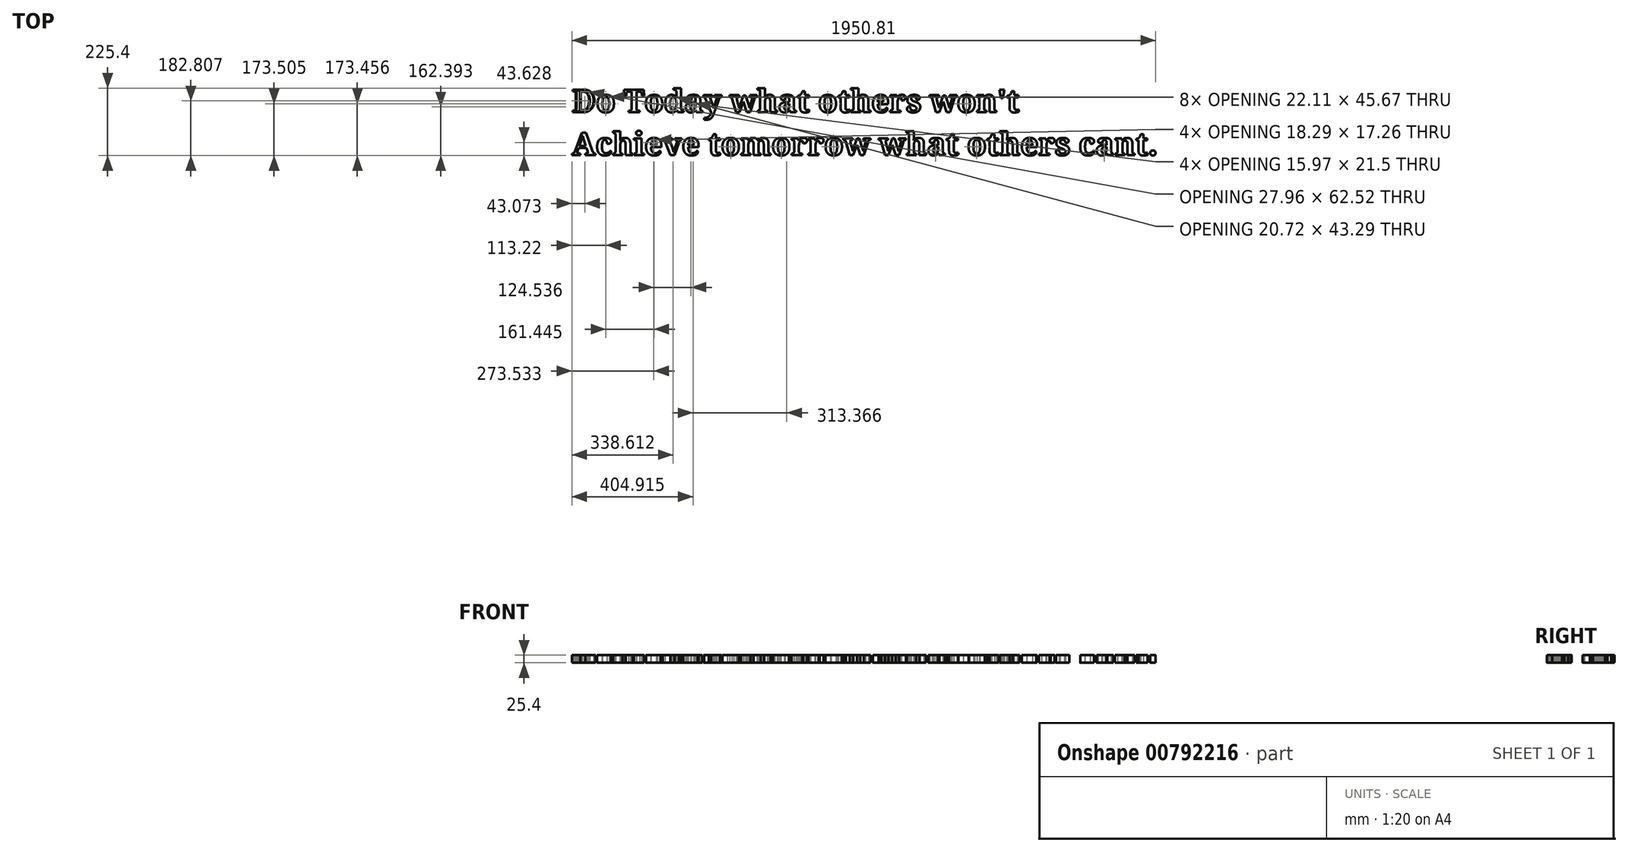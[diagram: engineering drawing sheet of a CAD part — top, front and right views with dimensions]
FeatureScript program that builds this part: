
annotation { "Feature Type Name" : "Feature", "Feature Type Description" : "" }
export const myFeature = defineFeature(function(context is Context, id is Id, definition is map)
    precondition{}
    {
        {
            var Q0;
            Q0=qCreatedBy(makeId("Top.planeOp"),FACE);
            var sketch = newSketch(context, id + "F0", { "sketchPlane" : qUnion([Q0])});
            skLineSegment(sketch, "E0.bottom", {"start": v(979.04, 38.1) * mm, "end": v(-979.04, 38.1) * mm, "construction": true});
            skLineSegment(sketch, "E0.top", {"start": v(979.04, -38.1) * mm, "end": v(-979.04, -38.1) * mm, "construction": true});
            skLineSegment(sketch, "E0.left", {"start": v(979.04, 38.1) * mm, "end": v(979.04, -38.1) * mm, "construction": true});
            skLineSegment(sketch, "E0.right", {"start": v(-979.04, 38.1) * mm, "end": v(-979.04, -38.1) * mm, "construction": true});
            skPoint(sketch, "E0.middle", {"position": v(0, 0) * mm});
            skText(sketch, "E1", { "text": "Do Today what others won\'t\nAchieve tomorrow what others cant.", "fontName": "NotoSerif-Bold.ttf"});
            const initialGuessF0  = {"E1": [-0.97904, -0.0381, 1, 0, 0.0762]};
            skSetInitialGuess(sketch, initialGuessF0);
            skSolve(sketch);
        }
        {
            var Q0;
            Q0 = qSketchRegion(id + "F0", true);
            extrude(context, id + "F1", {"entities" : qUnion([Q0]), "depth" : 25.4 * mm, "offsetDistance" : 25.4 * mm});
        }
        {
            var Q0;
            Q0=makeQuery(id+"F1.opExtrude","CAP_FACE",FACE,{"disambiguationData":[OSD([sQuery(id+"F0.wireOp",EDGE,"E1.sketch_text.stroke-0"),sQuery(id+"F0.wireOp",EDGE,"E1.sketch_text.stroke-1"),sQuery(id+"F0.wireOp",EDGE,"E1.sketch_text.stroke-2"),sQuery(id+"F0.wireOp",EDGE,"E1.sketch_text.stroke-3"),sQuery(id+"F0.wireOp",EDGE,"E1.sketch_text.stroke-4"),sQuery(id+"F0.wireOp",EDGE,"E1.sketch_text.stroke-5"),sQuery(id+"F0.wireOp",EDGE,"E1.sketch_text.stroke-6"),sQuery(id+"F0.wireOp",EDGE,"E1.sketch_text.stroke-7"),sQuery(id+"F0.wireOp",EDGE,"E1.sketch_text.stroke-8"),sQuery(id+"F0.wireOp",EDGE,"E1.sketch_text.stroke-9"),sQuery(id+"F0.wireOp",EDGE,"E1.sketch_text.stroke-10"),sQuery(id+"F0.wireOp",EDGE,"E1.sketch_text.stroke-11"),sQuery(id+"F0.wireOp",EDGE,"E1.sketch_text.stroke-12"),sQuery(id+"F0.wireOp",EDGE,"E1.sketch_text.stroke-13"),sQuery(id+"F0.wireOp",EDGE,"E1.sketch_text.stroke-14"),sQuery(id+"F0.wireOp",EDGE,"E1.sketch_text.stroke-15"),sQuery(id+"F0.wireOp",EDGE,"E1.sketch_text.stroke-16"),sQuery(id+"F0.wireOp",EDGE,"E1.sketch_text.stroke-17"),sQuery(id+"F0.wireOp",EDGE,"E1.sketch_text.stroke-18"),sQuery(id+"F0.wireOp",EDGE,"E1.sketch_text.stroke-19"),sQuery(id+"F0.wireOp",EDGE,"E1.sketch_text.stroke-20"),sQuery(id+"F0.wireOp",EDGE,"E1.sketch_text.stroke-21"),sQuery(id+"F0.wireOp",EDGE,"E1.sketch_text.stroke-22"),sQuery(id+"F0.wireOp",EDGE,"E1.sketch_text.stroke-23"),sQuery(id+"F0.wireOp",EDGE,"E1.sketch_text.stroke-24"),sQuery(id+"F0.wireOp",EDGE,"E1.sketch_text.stroke-25"),sQuery(id+"F0.wireOp",EDGE,"E1.sketch_text.stroke-26"),sQuery(id+"F0.wireOp",EDGE,"E1.sketch_text.stroke-27"),sQuery(id+"F0.wireOp",EDGE,"E1.sketch_text.stroke-28"),sQuery(id+"F0.wireOp",EDGE,"E1.sketch_text.stroke-29"),sQuery(id+"F0.wireOp",EDGE,"E1.sketch_text.stroke-30"),sQuery(id+"F0.wireOp",EDGE,"E1.sketch_text.stroke-31")])],"isStart":false});
            shell(context, id + "F2", {"entities" : qUnion([Q0]), "thickness" : 2.54 * mm});
        }
    });
